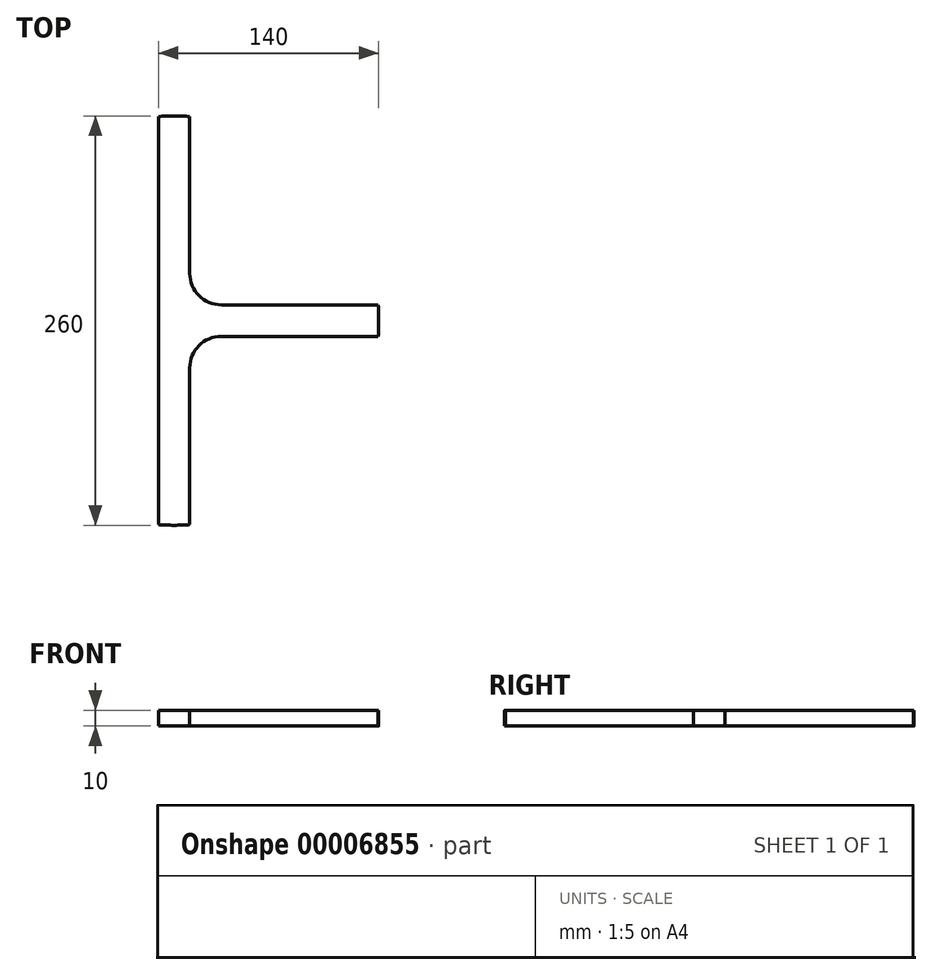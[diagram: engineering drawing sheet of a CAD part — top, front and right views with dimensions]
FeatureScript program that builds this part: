
annotation { "Feature Type Name" : "Feature", "Feature Type Description" : "" }
export const myFeature = defineFeature(function(context is Context, id is Id, definition is map)
    precondition{}
    {
        {
            var Q0;
            Q0=qCreatedBy(makeId("Top.planeOp"),FACE);
            var sketch = newSketch(context, id + "F0", { "sketchPlane" : qUnion([Q0])});
            skLineSegment(sketch, "E0.bottom", {"start": v(0.48, 229.76) * mm, "end": v(20.48, 229.76) * mm});
            skLineSegment(sketch, "E0.top", {"start": v(0.48, -30.24) * mm, "end": v(20.48, -30.24) * mm});
            skLineSegment(sketch, "E0.left", {"start": v(0.48, 229.76) * mm, "end": v(0.48, -30.24) * mm});
            skLineSegment(sketch, "E0.right", {"start": v(20.48, 229.76) * mm, "end": v(20.48, -30.24) * mm});
            skLineSegment(sketch, "E1.bottom", {"start": v(-119.52, 109.76) * mm, "end": v(140.48, 109.76) * mm});
            skLineSegment(sketch, "E1.top", {"start": v(-119.52, 89.76) * mm, "end": v(140.48, 89.76) * mm});
            skLineSegment(sketch, "E1.left", {"start": v(-119.52, 109.76) * mm, "end": v(-119.52, 89.76) * mm});
            skLineSegment(sketch, "E1.right", {"start": v(140.48, 109.76) * mm, "end": v(140.48, 89.76) * mm});
            skPoint(sketch, "E2", {"position": v(10.48, 229.76) * mm});
            skPoint(sketch, "E3", {"position": v(140.48, 99.76) * mm});
            skPoint(sketch, "E4", {"position": v(20.48, 99.76) * mm});
            skPoint(sketch, "E5", {"position": v(10.48, 109.76) * mm});
            skCircle(sketch, "E6", {"center": v(10.48, 99.76) * mm, "radius": 130 * mm});
            skSolve(sketch);
        }
        {
            var Q0;
            {var subQ0=sQuery(id+"F0.wireOp",EDGE,"E1.bottom");var subQ1=sQuery(id+"F0.wireOp",EDGE,"E0.left");var subQ2=makeQuery(id+"F0.imprint","INTERSECT",VERTEX,{"derivedFrom":[subQ1,subQ0]});Q0=makeQuery(id+"F0.imprint","IMPRINT",FACE,{"disambiguationData":[TD([[makeQuery(id+"F0.imprint","IMPRINT",EDGE,{"disambiguationData":[TD([[subQ2,-1.0]])],"derivedFrom":subQ1}),1.0]])]});}
            var Q1;
            {var subQ0=sQuery(id+"F0.wireOp",EDGE,"E6");var subQ5=sQuery(id+"F0.wireOp",EDGE,"E0.left");var subQ8=makeQuery(id+"F0.imprint","INTERSECT",VERTEX,{"disambiguationData":[OD(0.0)],"derivedFrom":[subQ5,subQ0]});Q1=makeQuery(id+"F0.imprint","IMPRINT",FACE,{"disambiguationData":[TD([[makeQuery(id+"F0.imprint","IMPRINT",EDGE,{"disambiguationData":[TD([[subQ8,-1.0]])],"derivedFrom":subQ5}),1.0]])]});}
            var Q2;
            {var subQ4=sQuery(id+"F0.wireOp",EDGE,"E1.bottom");var subQ6=sQuery(id+"F0.wireOp",EDGE,"E0.right");var subQ7=makeQuery(id+"F0.imprint","INTERSECT",VERTEX,{"derivedFrom":[subQ6,subQ4]});Q2=makeQuery(id+"F0.imprint","IMPRINT",FACE,{"disambiguationData":[TD([[makeQuery(id+"F0.imprint","IMPRINT",EDGE,{"disambiguationData":[TD([[subQ7,-1.0]])],"derivedFrom":subQ6}),1.0]])]});}
            var Q3;
            {var subQ0=sQuery(id+"F0.wireOp",EDGE,"E6");var subQ6=sQuery(id+"F0.wireOp",EDGE,"E0.left");var subQ7=makeQuery(id+"F0.imprint","INTERSECT",VERTEX,{"disambiguationData":[OD(1.0)],"derivedFrom":[subQ6,subQ0]});Q3=makeQuery(id+"F0.imprint","IMPRINT",FACE,{"disambiguationData":[TD([[makeQuery(id+"F0.imprint","IMPRINT",EDGE,{"disambiguationData":[TD([[subQ7,1.0]])],"derivedFrom":subQ6}),1.0]])]});}
            extrude(context, id + "F1", {"entities" : qUnion([Q0, Q1, Q2, Q3]), "depth" : 10 * mm});
        }
        {
            var Q0;
            Q0=makeQuery(id+"F1.opExtrude","SWEPT_EDGE",EDGE,{"disambiguationData":[OSD([sQuery(id+"F0.wireOp",EDGE,"E0.right"),sQuery(id+"F0.wireOp",EDGE,"E1.top")])]});
            var Q1;
            Q1=makeQuery(id+"F1.opExtrude","SWEPT_EDGE",EDGE,{"disambiguationData":[OSD([sQuery(id+"F0.wireOp",EDGE,"E0.right"),sQuery(id+"F0.wireOp",EDGE,"E1.bottom")])]});
            fillet(context, id + "F2", {"entities" : qUnion([Q0, Q1]), "radius" : 20 * mm, "tangentPropagation" : true, "allowEdgeOverflow" : false});
        }
    });
